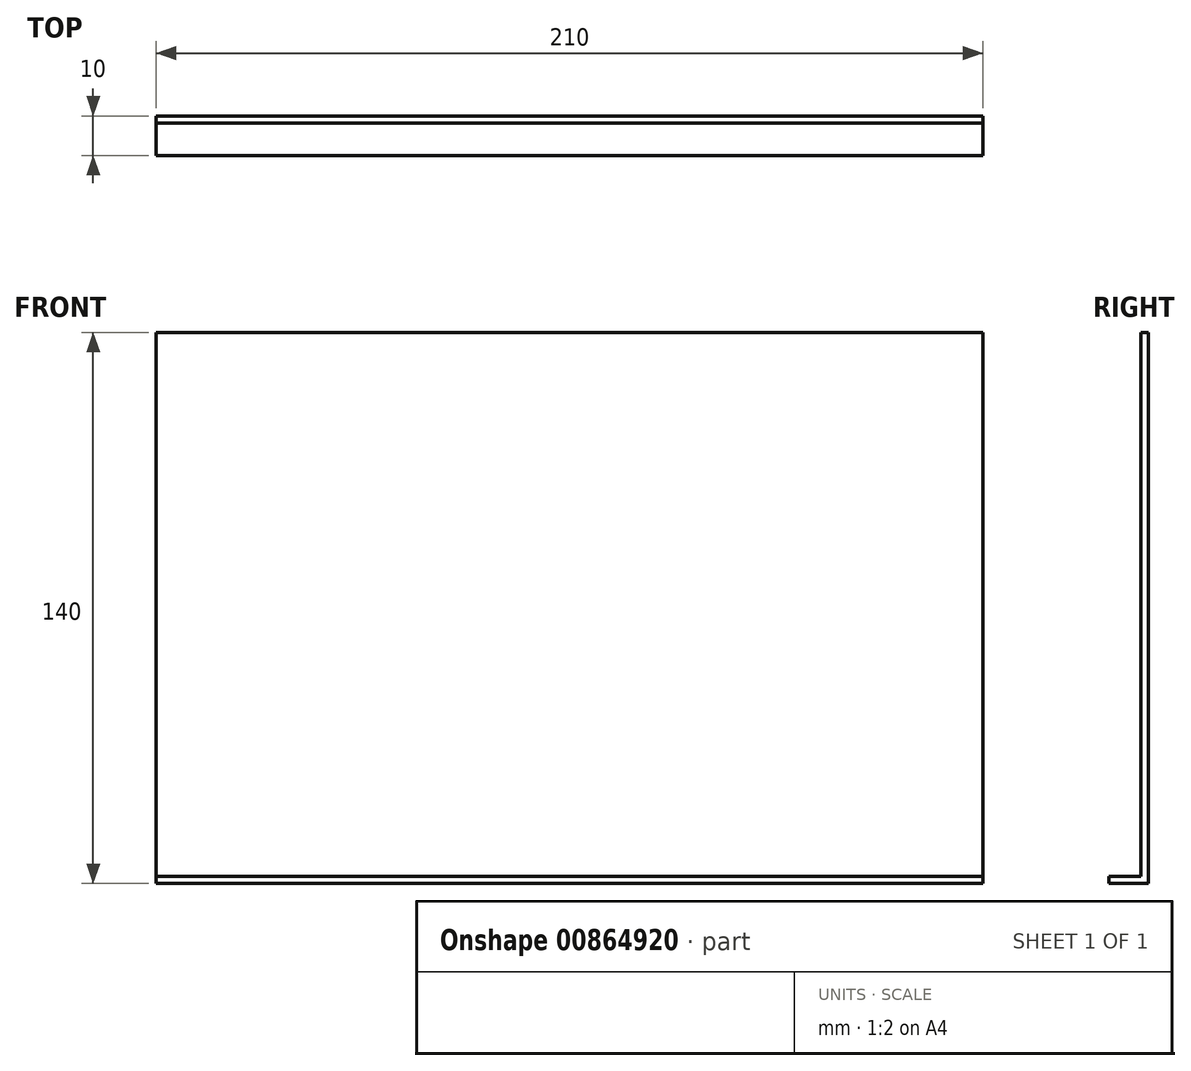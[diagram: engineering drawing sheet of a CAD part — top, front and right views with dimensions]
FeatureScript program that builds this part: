
annotation { "Feature Type Name" : "Feature", "Feature Type Description" : "" }
export const myFeature = defineFeature(function(context is Context, id is Id, definition is map)
    precondition{}
    {
        {
            var Q0;
            Q0=qCreatedBy(makeId("Front.planeOp"),FACE);
            var sketch = newSketch(context, id + "F0", { "sketchPlane" : qUnion([Q0])});
            skLineSegment(sketch, "E0.bottom", {"start": v(105, -70) * mm, "end": v(-105, -70) * mm});
            skLineSegment(sketch, "E0.top", {"start": v(105, 70) * mm, "end": v(-105, 70) * mm});
            skLineSegment(sketch, "E0.left", {"start": v(105, -70) * mm, "end": v(105, 70) * mm});
            skLineSegment(sketch, "E0.right", {"start": v(-105, -70) * mm, "end": v(-105, 70) * mm});
            skPoint(sketch, "E0.middle", {"position": v(0, 0) * mm});
            skLineSegment(sketch, "E1.bottom", {"start": v(-105, -70) * mm, "end": v(105, -70) * mm});
            skLineSegment(sketch, "E1.top", {"start": v(-105, -68.2) * mm, "end": v(105, -68.2) * mm});
            skLineSegment(sketch, "E1.left", {"start": v(-105, -70) * mm, "end": v(-105, -68.2) * mm});
            skLineSegment(sketch, "E1.right", {"start": v(105, -70) * mm, "end": v(105, -68.2) * mm});
            skSolve(sketch);
        }
        {
            var Q0;
            {var subQ0=sQuery(id+"F0.wireOp",EDGE,"E0.bottom");Q0=makeQuery(id+"F0.imprint","IMPRINT",FACE,{"disambiguationData":[TD([[makeQuery(id+"F0.imprint","IMPRINT",EDGE,{"derivedFrom":subQ0}),-1.0]])]});}
            extrude(context, id + "F1", {"entities" : qUnion([Q0]), "depth" : 10 * mm, "offsetDistance" : 25 * mm});
        }
        {
            var Q0;
            {var subQ0=sQuery(id+"F0.wireOp",EDGE,"E0.top");Q0=makeQuery(id+"F0.imprint","IMPRINT",FACE,{"disambiguationData":[TD([[makeQuery(id+"F0.imprint","IMPRINT",EDGE,{"derivedFrom":subQ0}),1.0]])]});}
            extrude(context, id + "F2", {"entities" : qUnion([Q0]), "operationType" : NewBodyOperationType.ADD, "depth" : 1.8 * mm, "offsetDistance" : 25 * mm});
        }
    });
